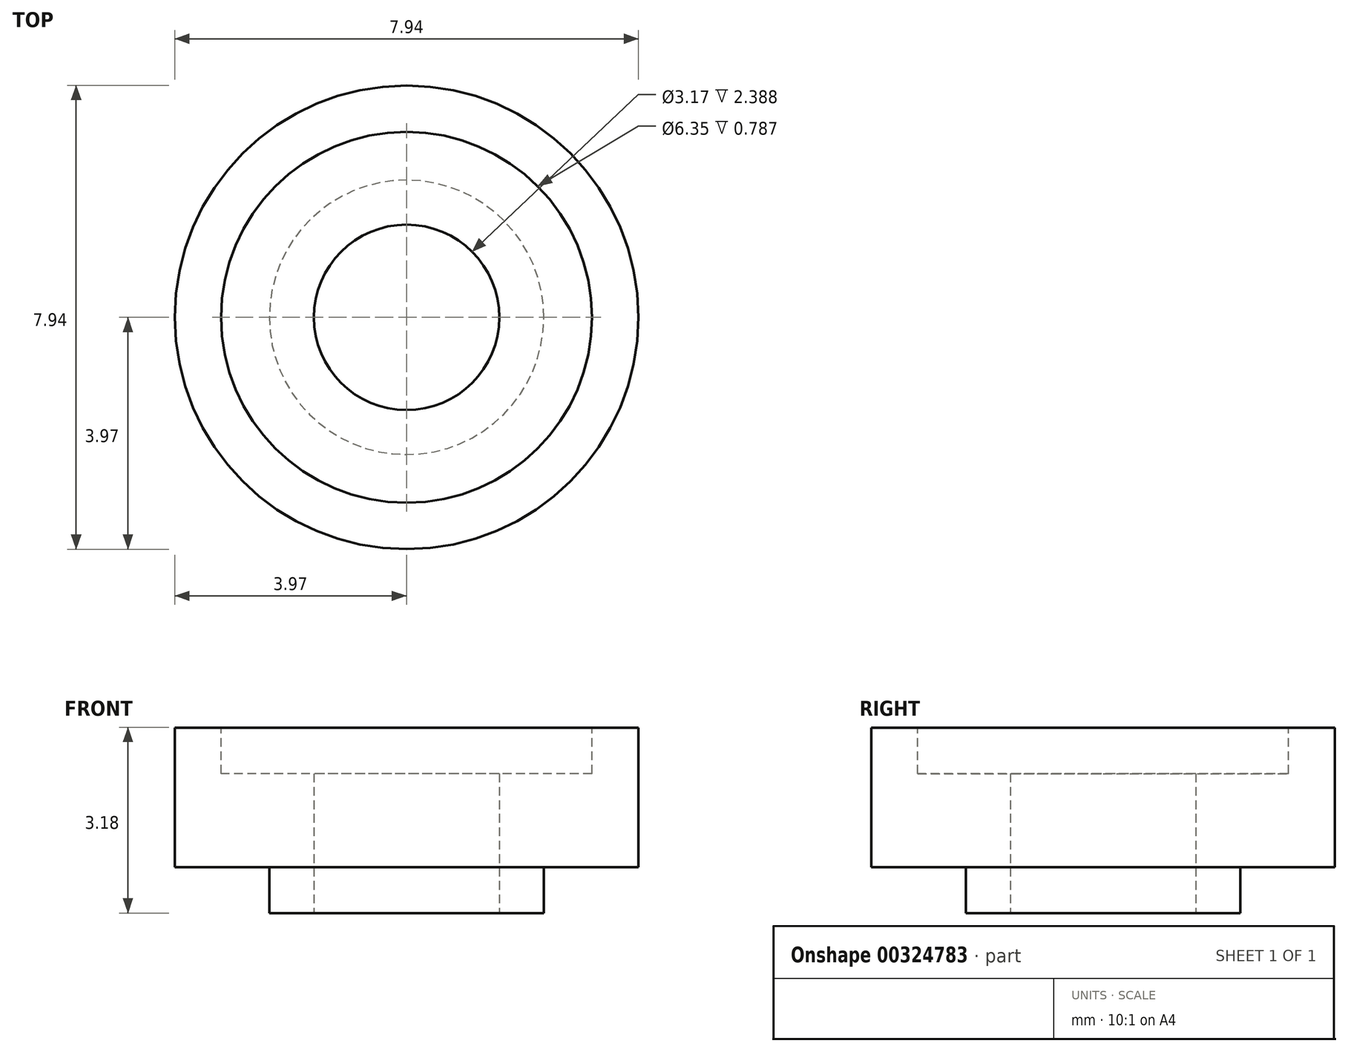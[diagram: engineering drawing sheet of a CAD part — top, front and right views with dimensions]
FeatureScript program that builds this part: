
annotation { "Feature Type Name" : "Feature", "Feature Type Description" : "" }
export const myFeature = defineFeature(function(context is Context, id is Id, definition is map)
    precondition{}
    {
        {
            var Q0;
            Q0=qCreatedBy(makeId("Top.planeOp"),FACE);
            var sketch = newSketch(context, id + "F0", { "sketchPlane" : qUnion([Q0])});
            skCircle(sketch, "E0", {"center": v(0, 0) * mm, "radius": 3.97 * mm});
            skCircle(sketch, "E1", {"center": v(0, 0) * mm, "radius": 1.59 * mm});
            skSolve(sketch);
        }
        {
            var Q0;
            Q0=makeQuery(id+"F0.imprint","IMPRINT",FACE,{"disambiguationData":[TD([[makeQuery(id+"F0.imprint","IMPRINT",EDGE,{"derivedFrom":sQuery(id+"F0.wireOp",EDGE,"E0")}),1.0]])]});
            extrude(context, id + "F1", {"entities" : qUnion([Q0]), "depth" : 3.17 * mm, "offsetDistance" : 25.4 * mm});
        }
        {
            var Q0;
            Q0=makeQuery(id+"F1.opExtrude","CAP_FACE",FACE,{"disambiguationData":[OSD([sQuery(id+"F0.wireOp",EDGE,"E0"),sQuery(id+"F0.wireOp",EDGE,"E1")])],"isStart":false});
            var sketch = newSketch(context, id + "F2", { "sketchPlane" : qUnion([Q0])});
            skCircle(sketch, "E2", {"center": v(0, 0) * mm, "radius": 3.18 * mm});
            skSolve(sketch);
        }
        {
            var Q0;
            Q0=makeQuery(id+"F2.imprint","IMPRINT",FACE,{"disambiguationData":[TD([[makeQuery(id+"F2.imprint","IMPRINT",EDGE,{"derivedFrom":sQuery(id+"F2.wireOp",EDGE,"E2")}),1.0]])]});
            extrude(context, id + "F3", {"entities" : qUnion([Q0]), "operationType" : NewBodyOperationType.REMOVE, "oppositeDirection" : true, "depth" : 0.79 * mm, "offsetDistance" : 25.4 * mm});
        }
        {
            var Q0;
            Q0=makeQuery(id+"F1.opExtrude","CAP_FACE",FACE,{"disambiguationData":[OSD([sQuery(id+"F0.wireOp",EDGE,"E0"),sQuery(id+"F0.wireOp",EDGE,"E1")])],"isStart":true});
            var sketch = newSketch(context, id + "F4", { "sketchPlane" : qUnion([Q0])});
            skCircle(sketch, "E3", {"center": v(0, 0) * mm, "radius": 2.35 * mm});
            skCircle(sketch, "E4", {"center": v(0, 0) * mm, "radius": 3.97 * mm});
            skSolve(sketch);
        }
        {
            var Q0;
            Q0=makeQuery(id+"F4.imprint","IMPRINT",FACE,{"disambiguationData":[TD([[makeQuery(id+"F4.imprint","IMPRINT",EDGE,{"derivedFrom":sQuery(id+"F4.wireOp",EDGE,"E3")}),-1.0]])]});
            extrude(context, id + "F5", {"entities" : qUnion([Q0]), "operationType" : NewBodyOperationType.REMOVE, "oppositeDirection" : true, "depth" : 0.79 * mm, "offsetDistance" : 25.4 * mm});
        }
    });
